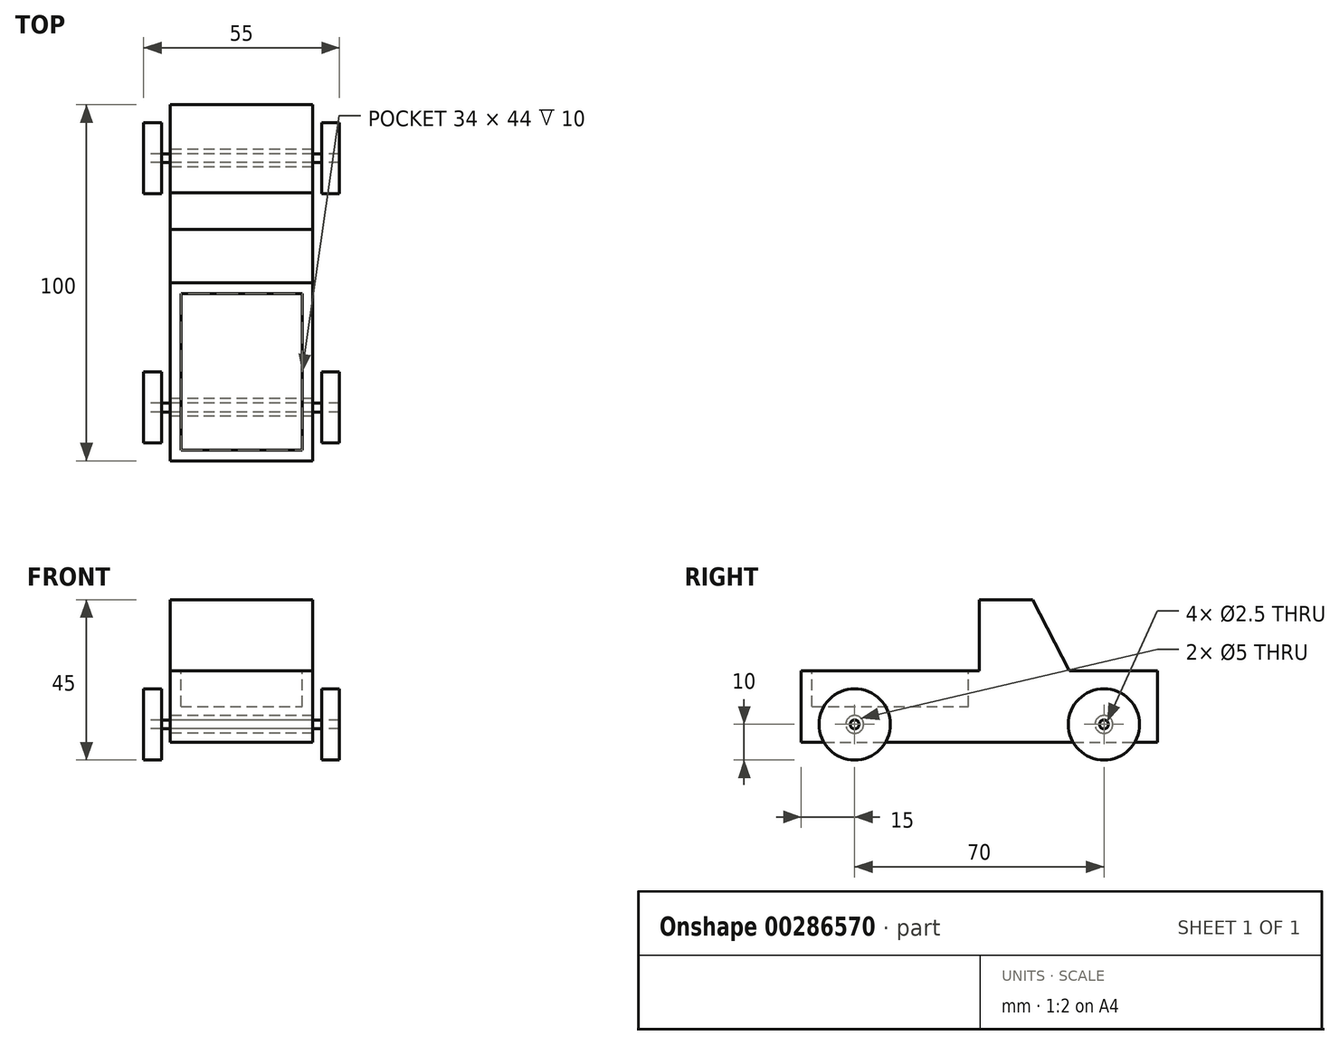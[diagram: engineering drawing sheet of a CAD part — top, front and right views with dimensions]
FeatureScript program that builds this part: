
annotation { "Feature Type Name" : "Feature", "Feature Type Description" : "" }
export const myFeature = defineFeature(function(context is Context, id is Id, definition is map)
    precondition{}
    {
        {
            var Q0;
            Q0=qCreatedBy(makeId("Front.planeOp"),FACE);
            var sketch = newSketch(context, id + "F0", { "sketchPlane" : qUnion([Q0])});
            skLineSegment(sketch, "E0.bottom", {"start": v(-20, 10) * mm, "end": v(20, 10) * mm});
            skLineSegment(sketch, "E0.top", {"start": v(-20, -10) * mm, "end": v(20, -10) * mm});
            skLineSegment(sketch, "E0.left", {"start": v(-20, 10) * mm, "end": v(-20, -10) * mm});
            skLineSegment(sketch, "E0.right", {"start": v(20, 10) * mm, "end": v(20, -10) * mm});
            skPoint(sketch, "E0.middle", {"position": v(0, 0) * mm});
            skSolve(sketch);
        }
        {
            var Q0;
            Q0 = qSketchRegion(id + "F0", true);
            extrude(context, id + "F1", {"entities" : qUnion([Q0]), "depth" : 50 * mm});
        }
        {
            var Q0;
            Q0=makeQuery(id+"F1.opExtrude","CAP_FACE",FACE,{"disambiguationData":[OSD([sQuery(id+"F0.wireOp",EDGE,"E0.bottom"),sQuery(id+"F0.wireOp",EDGE,"E0.top"),sQuery(id+"F0.wireOp",EDGE,"E0.left"),sQuery(id+"F0.wireOp",EDGE,"E0.right")])],"isStart":true});
            extrude(context, id + "F2", {"entities" : qUnion([Q0]), "operationType" : NewBodyOperationType.ADD, "depth" : 50 * mm});
        }
        {
            var Q0;
            Q0=qCreatedBy(makeId("Right.planeOp"),FACE);
            var sketch = newSketch(context, id + "F3", { "sketchPlane" : qUnion([Q0])});
            skLineSegment(sketch, "E1.bottom", {"start": v(0, 10) * mm, "end": v(15, 10) * mm});
            skLineSegment(sketch, "E1.top", {"start": v(0, 30) * mm, "end": v(15, 30) * mm});
            skLineSegment(sketch, "E1.left", {"start": v(0, 10) * mm, "end": v(0, 30) * mm});
            skLineSegment(sketch, "E1.right", {"start": v(15, 10) * mm, "end": v(15, 30) * mm});
            skSolve(sketch);
        }
        {
            var Q0;
            Q0 = qSketchRegion(id + "F3", true);
            extrude(context, id + "F4", {"entities" : qUnion([Q0]), "operationType" : NewBodyOperationType.ADD, "depth" : 20 * mm});
        }
        {
            var Q0;
            Q0=makeQuery(id+"F4.opExtrude","CAP_FACE",FACE,{"disambiguationData":[OSD([sQuery(id+"F3.wireOp",EDGE,"E1.bottom"),sQuery(id+"F3.wireOp",EDGE,"E1.top"),sQuery(id+"F3.wireOp",EDGE,"E1.left"),sQuery(id+"F3.wireOp",EDGE,"E1.right")])],"isStart":true});
            extrude(context, id + "F5", {"entities" : qUnion([Q0]), "operationType" : NewBodyOperationType.ADD, "depth" : 20 * mm});
        }
        {
            var Q0;
            {var subQ0=sQuery(id+"F0.wireOp",EDGE,"E0.left");Q0=makeQuery(id+"F5.boolean.opBoolean","MERGE",FACE,{"derivedFrom":[makeQuery(id+"F2.boolean.opBoolean","MERGE",FACE,{"derivedFrom":[makeQuery(id+"F1.opExtrude","SWEPT_FACE",FACE,{"disambiguationData":[OSD([subQ0])]}),makeQuery(id+"F2.opExtrude","SWEPT_FACE",FACE,{"disambiguationData":[OSD([subQ0])]})]}),makeQuery(id+"F5.opExtrude","CAP_FACE",FACE,{"disambiguationData":[OSD([sQuery(id+"F3.wireOp",EDGE,"E1.bottom"),sQuery(id+"F3.wireOp",EDGE,"E1.top"),sQuery(id+"F3.wireOp",EDGE,"E1.left"),sQuery(id+"F3.wireOp",EDGE,"E1.right")])],"isStart":false})]});}
            var sketch = newSketch(context, id + "F6", { "sketchPlane" : qUnion([Q0])});
            skLineSegment(sketch, "E2", {"start": v(-15, 30) * mm, "end": v(-25.3, 10) * mm});
            skLineSegment(sketch, "E3", {"start": v(-25.3, 10) * mm, "end": v(-15, 10) * mm});
            skLineSegment(sketch, "E4", {"start": v(-15, 10) * mm, "end": v(-15, 30) * mm});
            skSolve(sketch);
        }
        {
            var Q0;
            Q0 = qSketchRegion(id + "F6", true);
            extrude(context, id + "F7", {"entities" : qUnion([Q0]), "operationType" : NewBodyOperationType.ADD, "oppositeDirection" : true, "depth" : 40 * mm});
        }
        {
            var Q0;
            {var subQ0=sQuery(id+"F0.wireOp",EDGE,"E0.left");Q0=makeQuery(id+"F7.boolean.opBoolean","MERGE",FACE,{"derivedFrom":[makeQuery(id+"F5.boolean.opBoolean","MERGE",FACE,{"derivedFrom":[makeQuery(id+"F2.boolean.opBoolean","MERGE",FACE,{"derivedFrom":[makeQuery(id+"F1.opExtrude","SWEPT_FACE",FACE,{"disambiguationData":[OSD([subQ0])]}),makeQuery(id+"F2.opExtrude","SWEPT_FACE",FACE,{"disambiguationData":[OSD([subQ0])]})]}),makeQuery(id+"F5.opExtrude","CAP_FACE",FACE,{"disambiguationData":[OSD([sQuery(id+"F3.wireOp",EDGE,"E1.bottom"),sQuery(id+"F3.wireOp",EDGE,"E1.top"),sQuery(id+"F3.wireOp",EDGE,"E1.left"),sQuery(id+"F3.wireOp",EDGE,"E1.right")])],"isStart":false})]}),makeQuery(id+"F7.opExtrude","CAP_FACE",FACE,{"disambiguationData":[OSD([sQuery(id+"F6.wireOp",EDGE,"E2"),sQuery(id+"F6.wireOp",EDGE,"E3"),sQuery(id+"F6.wireOp",EDGE,"E4")])],"isStart":true})]});}
            var sketch = newSketch(context, id + "F8", { "sketchPlane" : qUnion([Q0])});
            skCircle(sketch, "E5", {"center": v(-35, -5) * mm, "radius": 2.5 * mm});
            skSolve(sketch);
        }
        {
            var Q0;
            Q0 = qSketchRegion(id + "F8", true);
            extrude(context, id + "F9", {"entities" : qUnion([Q0]), "operationType" : NewBodyOperationType.REMOVE, "endBound" : BoundingType.THROUGH_ALL, "oppositeDirection" : true, "depth" : 25 * mm});
        }
        {
            var Q0;
            {var subQ0=sQuery(id+"F0.wireOp",EDGE,"E0.left");Q0=makeQuery(id+"F7.boolean.opBoolean","MERGE",FACE,{"derivedFrom":[makeQuery(id+"F5.boolean.opBoolean","MERGE",FACE,{"derivedFrom":[makeQuery(id+"F2.boolean.opBoolean","MERGE",FACE,{"derivedFrom":[makeQuery(id+"F1.opExtrude","SWEPT_FACE",FACE,{"disambiguationData":[OSD([subQ0])]}),makeQuery(id+"F2.opExtrude","SWEPT_FACE",FACE,{"disambiguationData":[OSD([subQ0])]})]}),makeQuery(id+"F5.opExtrude","CAP_FACE",FACE,{"disambiguationData":[OSD([sQuery(id+"F3.wireOp",EDGE,"E1.bottom"),sQuery(id+"F3.wireOp",EDGE,"E1.top"),sQuery(id+"F3.wireOp",EDGE,"E1.left"),sQuery(id+"F3.wireOp",EDGE,"E1.right")])],"isStart":false})]}),makeQuery(id+"F7.opExtrude","CAP_FACE",FACE,{"disambiguationData":[OSD([sQuery(id+"F6.wireOp",EDGE,"E2"),sQuery(id+"F6.wireOp",EDGE,"E3"),sQuery(id+"F6.wireOp",EDGE,"E4")])],"isStart":true})]});}
            var sketch = newSketch(context, id + "F10", { "sketchPlane" : qUnion([Q0])});
            skCircle(sketch, "E6", {"center": v(35, -5) * mm, "radius": 2.5 * mm});
            skSolve(sketch);
        }
        {
            var Q0;
            Q0 = qSketchRegion(id + "F10", true);
            extrude(context, id + "F11", {"entities" : qUnion([Q0]), "operationType" : NewBodyOperationType.REMOVE, "endBound" : BoundingType.THROUGH_ALL, "oppositeDirection" : true, "depth" : 25 * mm});
        }
        {
            var Q0;
            {var subQ1=sQuery(id+"F3.wireOp",EDGE,"E1.left");var subQ6=sQuery(id+"F0.wireOp",EDGE,"E0.bottom");Q0=makeQuery(id+"F5.boolean.opBoolean","SPLIT",FACE,{"disambiguationData":[TD([makeQuery(id+"F4.opExtrude","SWEPT_FACE",FACE,{"disambiguationData":[OSD([subQ1])]})])],"derivedFrom":makeQuery(id+"F2.boolean.opBoolean","MERGE",FACE,{"derivedFrom":[makeQuery(id+"F1.opExtrude","SWEPT_FACE",FACE,{"disambiguationData":[OSD([subQ6])]}),makeQuery(id+"F2.opExtrude","SWEPT_FACE",FACE,{"disambiguationData":[OSD([subQ6])]})]})});}
            var sketch = newSketch(context, id + "F12", { "sketchPlane" : qUnion([Q0])});
            skLineSegment(sketch, "E7.0", {"start": v(-17, -47) * mm, "end": v(-17, -3) * mm});
            skLineSegment(sketch, "E7.1", {"start": v(-17, -47) * mm, "end": v(17, -47) * mm});
            skLineSegment(sketch, "E7.2", {"start": v(17, -47) * mm, "end": v(17, -3) * mm});
            skLineSegment(sketch, "E7.3", {"start": v(17, -3) * mm, "end": v(-17, -3) * mm});
            skSolve(sketch);
        }
        {
            var Q0;
            Q0=makeQuery(id+"F12.imprint","IMPRINT",FACE,{"disambiguationData":[TD([[makeQuery(id+"F12.imprint","IMPRINT",EDGE,{"derivedFrom":sQuery(id+"F12.wireOp",EDGE,"E7.0")}),-1.0]])]});
            extrude(context, id + "F13", {"entities" : qUnion([Q0]), "operationType" : NewBodyOperationType.REMOVE, "oppositeDirection" : true, "depth" : 10 * mm});
        }
        {
            var Q0;
            Q0=qCreatedBy(makeId("Right.planeOp"),FACE);
            var sketch = newSketch(context, id + "F14", { "sketchPlane" : qUnion([Q0])});
            skCircle(sketch, "E8", {"center": v(-35, -5) * mm, "radius": 1.25 * mm});
            skSolve(sketch);
        }
        {
            var Q0;
            Q0=makeQuery(id+"F14.imprint","IMPRINT",FACE,{"disambiguationData":[TD([[makeQuery(id+"F14.imprint","IMPRINT",EDGE,{"derivedFrom":sQuery(id+"F14.wireOp",EDGE,"E8")}),1.0]])]});
            extrude(context, id + "F15", {"entities" : qUnion([Q0]), "depth" : 22.5 * mm});
        }
        {
            var Q0;
            Q0=makeQuery(id+"F15.opExtrude","CAP_FACE",FACE,{"disambiguationData":[OSD([sQuery(id+"F14.wireOp",EDGE,"E8")])],"isStart":true});
            extrude(context, id + "F16", {"entities" : qUnion([Q0]), "operationType" : NewBodyOperationType.ADD, "depth" : 22.5 * mm});
        }
        {
            var Q0;
            Q0=makeQuery(id+"F15.opExtrude","SWEPT_BODY",BODY,{"disambiguationData":[OSD([sQuery(id+"F14.wireOp",EDGE,"E8")])]});
            transform(context, id + "F17", {"entities" : qUnion([Q0]), "transformType" : TransformType.TRANSLATION_3D, "dx" : 0 * mm, "dy" : 70 * mm, "dz" : 0 * mm, "makeCopy" : true});
        }
        {
            var Q0;
            Q0=makeQuery(id+"F15.opExtrude","CAP_FACE",FACE,{"disambiguationData":[OSD([sQuery(id+"F14.wireOp",EDGE,"E8")])],"isStart":false});
            var sketch = newSketch(context, id + "F18", { "sketchPlane" : qUnion([Q0])});
            skCircle(sketch, "E9", {"center": v(-35, -5) * mm, "radius": 10 * mm});
            skSolve(sketch);
        }
        {
            var Q0;
            Q0=makeQuery(id+"F18.imprint","IMPRINT",FACE,{"disambiguationData":[TD([[makeQuery(id+"F18.imprint","IMPRINT",EDGE,{"derivedFrom":sQuery(id+"F18.wireOp",EDGE,"E9")}),1.0]])]});
            extrude(context, id + "F19", {"entities" : qUnion([Q0]), "depth" : 5 * mm});
        }
        {
            var Q0;
            Q0=makeQuery(id+"F19.opExtrude","SWEPT_BODY",BODY,{"disambiguationData":[OSD([sQuery(id+"F14.wireOp",EDGE,"E8"),sQuery(id+"F18.wireOp",EDGE,"E9")])]});
            transform(context, id + "F20", {"entities" : qUnion([Q0]), "transformType" : TransformType.TRANSLATION_3D, "dx" : 0 * mm, "dy" : 70 * mm, "dz" : 0 * mm, "makeCopy" : true});
        }
        {
            var Q0;
            Q0=makeQuery(id+"F19.opExtrude","SWEPT_BODY",BODY,{"disambiguationData":[OSD([sQuery(id+"F14.wireOp",EDGE,"E8"),sQuery(id+"F18.wireOp",EDGE,"E9")])]});
            transform(context, id + "F21", {"entities" : qUnion([Q0]), "transformType" : TransformType.TRANSLATION_3D, "dx" : -50 * mm, "dy" : 0 * mm, "dz" : 0 * mm, "makeCopy" : true});
        }
        {
            var Q0;
            Q0=makeQuery(id+"F19.opExtrude","SWEPT_BODY",BODY,{"disambiguationData":[OSD([sQuery(id+"F14.wireOp",EDGE,"E8"),sQuery(id+"F18.wireOp",EDGE,"E9")])]});
            transform(context, id + "F22", {"entities" : qUnion([Q0]), "transformType" : TransformType.TRANSLATION_3D, "dx" : -50 * mm, "dy" : 70 * mm, "dz" : 0 * mm, "makeCopy" : true});
        }
    });
